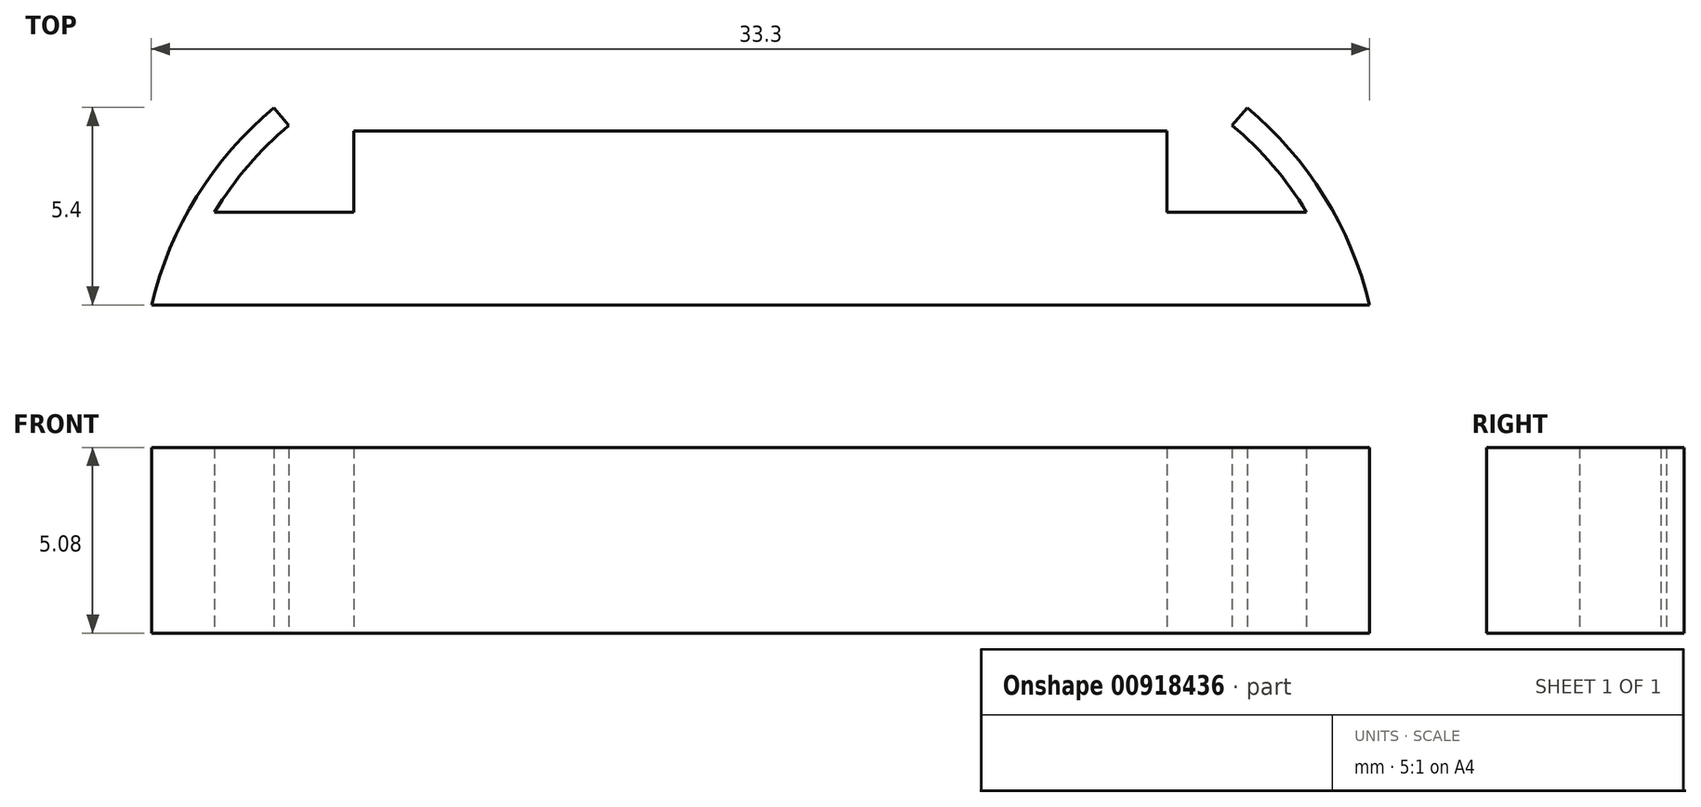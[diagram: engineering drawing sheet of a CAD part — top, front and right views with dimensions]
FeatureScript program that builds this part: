
annotation { "Feature Type Name" : "Feature", "Feature Type Description" : "" }
export const myFeature = defineFeature(function(context is Context, id is Id, definition is map)
    precondition{}
    {
        {
            var Q0;
            Q0=qCreatedBy(makeId("Top.planeOp"),FACE);
            var sketch = newSketch(context, id + "F0", { "sketchPlane" : qUnion([Q0])});
            skLineSegment(sketch, "E0", {"start": v(0, 0) * mm, "end": v(16.65, 0) * mm});
            skLineSegment(sketch, "E1", {"start": v(0, 0) * mm, "end": v(0, 4.76) * mm});
            skLineSegment(sketch, "E2", {"start": v(0, 4.76) * mm, "end": v(11.11, 4.76) * mm});
            skLineSegment(sketch, "E3", {"start": v(11.11, 4.76) * mm, "end": v(11.11, 2.54) * mm});
            skLineSegment(sketch, "E4", {"start": v(11.11, 2.54) * mm, "end": v(14.92, 2.54) * mm});
            skArc(sketch, "E5", {"start": v(14.92, 2.54) * mm, "mid": v(14, 3.8) * mm, "end": v(12.9, 4.91) * mm});
            skArc(sketch, "E6", {"start": v(16.65, 0) * mm, "mid": v(15.4, 2.97) * mm, "end": v(13.3, 5.4) * mm});
            skLineSegment(sketch, "E7", {"start": v(13.3, 5.4) * mm, "end": v(12.9, 4.91) * mm});
            skSolve(sketch);
        }
        {
            var Q0;
            Q0=makeQuery(id+"F0.imprint","IMPRINT",FACE,{"disambiguationData":[TD([[makeQuery(id+"F0.imprint","IMPRINT",EDGE,{"derivedFrom":sQuery(id+"F0.wireOp",EDGE,"E0")}),1.0]])]});
            extrude(context, id + "F1", {"entities" : qUnion([Q0]), "depth" : 5.08 * mm, "offsetDistance" : 25.4 * mm});
        }
        {
            var Q0;
            Q0=makeQuery(id+"F1.opExtrude","SWEPT_BODY",BODY,{"disambiguationData":[OSD([sQuery(id+"F0.wireOp",EDGE,"E0"),sQuery(id+"F0.wireOp",EDGE,"E1"),sQuery(id+"F0.wireOp",EDGE,"E2"),sQuery(id+"F0.wireOp",EDGE,"E3"),sQuery(id+"F0.wireOp",EDGE,"E4"),sQuery(id+"F0.wireOp",EDGE,"E5"),sQuery(id+"F0.wireOp",EDGE,"E6"),sQuery(id+"F0.wireOp",EDGE,"E7")])]});
            var Q1;
            Q1=makeQuery(id+"F1.opExtrude","SWEPT_FACE",FACE,{"disambiguationData":[OSD([sQuery(id+"F0.wireOp",EDGE,"E1")])]});
            mirror(context, id + "F2", {"operationType" : NewBodyOperationType.ADD, "entities" : qUnion([Q0]), "mirrorPlane" : qUnion([Q1])});
        }
    });
